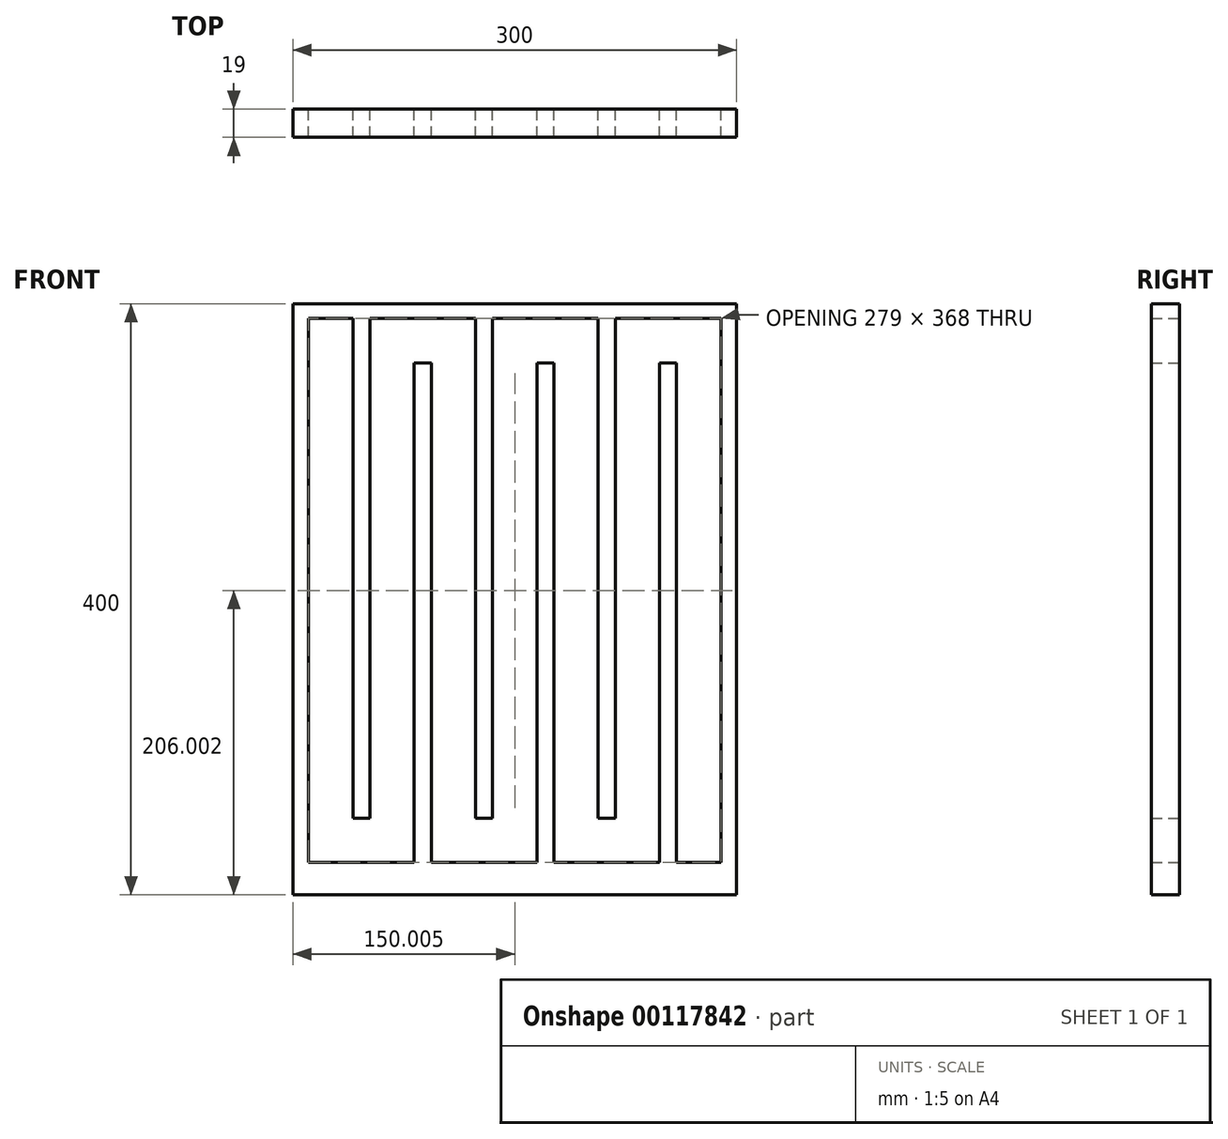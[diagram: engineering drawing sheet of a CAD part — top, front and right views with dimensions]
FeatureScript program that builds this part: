
annotation { "Feature Type Name" : "Feature", "Feature Type Description" : "" }
export const myFeature = defineFeature(function(context is Context, id is Id, definition is map)
    precondition{}
    {
        {
            var Q0;
            Q0=qCreatedBy(makeId("Front.planeOp"),FACE);
            var sketch = newSketch(context, id + "F0", { "sketchPlane" : qUnion([Q0])});
            skLineSegment(sketch, "E0.bottom", {"start": v(-184.2, 201.97) * mm, "end": v(115.8, 201.97) * mm});
            skLineSegment(sketch, "E0.top", {"start": v(-184.2, -198.03) * mm, "end": v(115.8, -198.03) * mm});
            skLineSegment(sketch, "E0.left", {"start": v(-184.2, 201.97) * mm, "end": v(-184.2, -198.03) * mm});
            skLineSegment(sketch, "E0.right", {"start": v(115.8, 201.97) * mm, "end": v(115.8, -198.03) * mm});
            skSolve(sketch);
        }
        {
            var Q0;
            Q0 = qSketchRegion(id + "F0", true);
            extrude(context, id + "F1", {"entities" : qUnion([Q0]), "depth" : 19 * mm});
        }
        {
            var Q0;
            Q0=makeQuery(id+"F1.opExtrude","CAP_FACE",FACE,{"disambiguationData":[OSD([sQuery(id+"F0.wireOp",EDGE,"E0.bottom"),sQuery(id+"F0.wireOp",EDGE,"E0.top"),sQuery(id+"F0.wireOp",EDGE,"E0.left"),sQuery(id+"F0.wireOp",EDGE,"E0.right")])],"isStart":true});
            var sketch = newSketch(context, id + "F2", { "sketchPlane" : qUnion([Q0])});
            skLineSegment(sketch, "E1", {"start": v(-105.3, -176.03) * mm, "end": v(-75.3, -176.03) * mm});
            skLineSegment(sketch, "E2", {"start": v(-75.3, -176.03) * mm, "end": v(-75.3, 161.97) * mm});
            skLineSegment(sketch, "E3", {"start": v(-75.3, 161.97) * mm, "end": v(-63.8, 161.97) * mm});
            skLineSegment(sketch, "E4", {"start": v(-63.8, 161.97) * mm, "end": v(-63.8, -176.03) * mm});
            skLineSegment(sketch, "E5", {"start": v(-63.8, -176.03) * mm, "end": v(7.7, -176.03) * mm});
            skLineSegment(sketch, "E6", {"start": v(7.7, -176.03) * mm, "end": v(7.7, 161.97) * mm});
            skLineSegment(sketch, "E7", {"start": v(7.7, 161.97) * mm, "end": v(19.2, 161.97) * mm});
            skLineSegment(sketch, "E8", {"start": v(19.2, 161.97) * mm, "end": v(19.2, -176.03) * mm});
            skLineSegment(sketch, "E9", {"start": v(19.2, -176.03) * mm, "end": v(90.7, -176.03) * mm});
            skLineSegment(sketch, "E10", {"start": v(90.7, -176.03) * mm, "end": v(90.7, 161.97) * mm});
            skLineSegment(sketch, "E11", {"start": v(90.7, 161.97) * mm, "end": v(102.2, 161.97) * mm});
            skLineSegment(sketch, "E12", {"start": v(102.2, 161.97) * mm, "end": v(102.2, -176.03) * mm});
            skLineSegment(sketch, "E13", {"start": v(102.2, -176.03) * mm, "end": v(173.7, -176.03) * mm});
            skLineSegment(sketch, "E14", {"start": v(173.7, -176.03) * mm, "end": v(173.7, 191.97) * mm});
            skLineSegment(sketch, "E15", {"start": v(173.7, 191.97) * mm, "end": v(143.7, 191.97) * mm});
            skLineSegment(sketch, "E16", {"start": v(143.7, 191.97) * mm, "end": v(143.7, -146.03) * mm});
            skLineSegment(sketch, "E17", {"start": v(143.7, -146.03) * mm, "end": v(132.2, -146.03) * mm});
            skLineSegment(sketch, "E18", {"start": v(132.2, -146.03) * mm, "end": v(132.2, 191.97) * mm});
            skLineSegment(sketch, "E19", {"start": v(132.2, 191.97) * mm, "end": v(60.7, 191.97) * mm});
            skLineSegment(sketch, "E20", {"start": v(60.7, 191.97) * mm, "end": v(60.7, -146.03) * mm});
            skLineSegment(sketch, "E21", {"start": v(60.7, -146.03) * mm, "end": v(49.2, -146.03) * mm});
            skLineSegment(sketch, "E22", {"start": v(49.2, -146.03) * mm, "end": v(49.2, 191.97) * mm});
            skLineSegment(sketch, "E23", {"start": v(49.2, 191.97) * mm, "end": v(-22.3, 191.97) * mm});
            skLineSegment(sketch, "E24", {"start": v(-22.3, 191.97) * mm, "end": v(-22.3, -146.03) * mm});
            skLineSegment(sketch, "E25", {"start": v(-22.3, -146.03) * mm, "end": v(-33.8, -146.03) * mm});
            skLineSegment(sketch, "E26", {"start": v(-33.8, -146.03) * mm, "end": v(-33.8, 191.97) * mm});
            skLineSegment(sketch, "E27", {"start": v(-33.8, 191.97) * mm, "end": v(-105.3, 191.97) * mm});
            skLineSegment(sketch, "E28", {"start": v(-105.3, 191.97) * mm, "end": v(-105.3, -176.03) * mm});
            skSolve(sketch);
        }
        {
            var Q0;
            Q0 = qSketchRegion(id + "F2", true);
            extrude(context, id + "F3", {"entities" : qUnion([Q0]), "operationType" : NewBodyOperationType.REMOVE, "oppositeDirection" : true, "depth" : 19 * mm});
        }
    });
